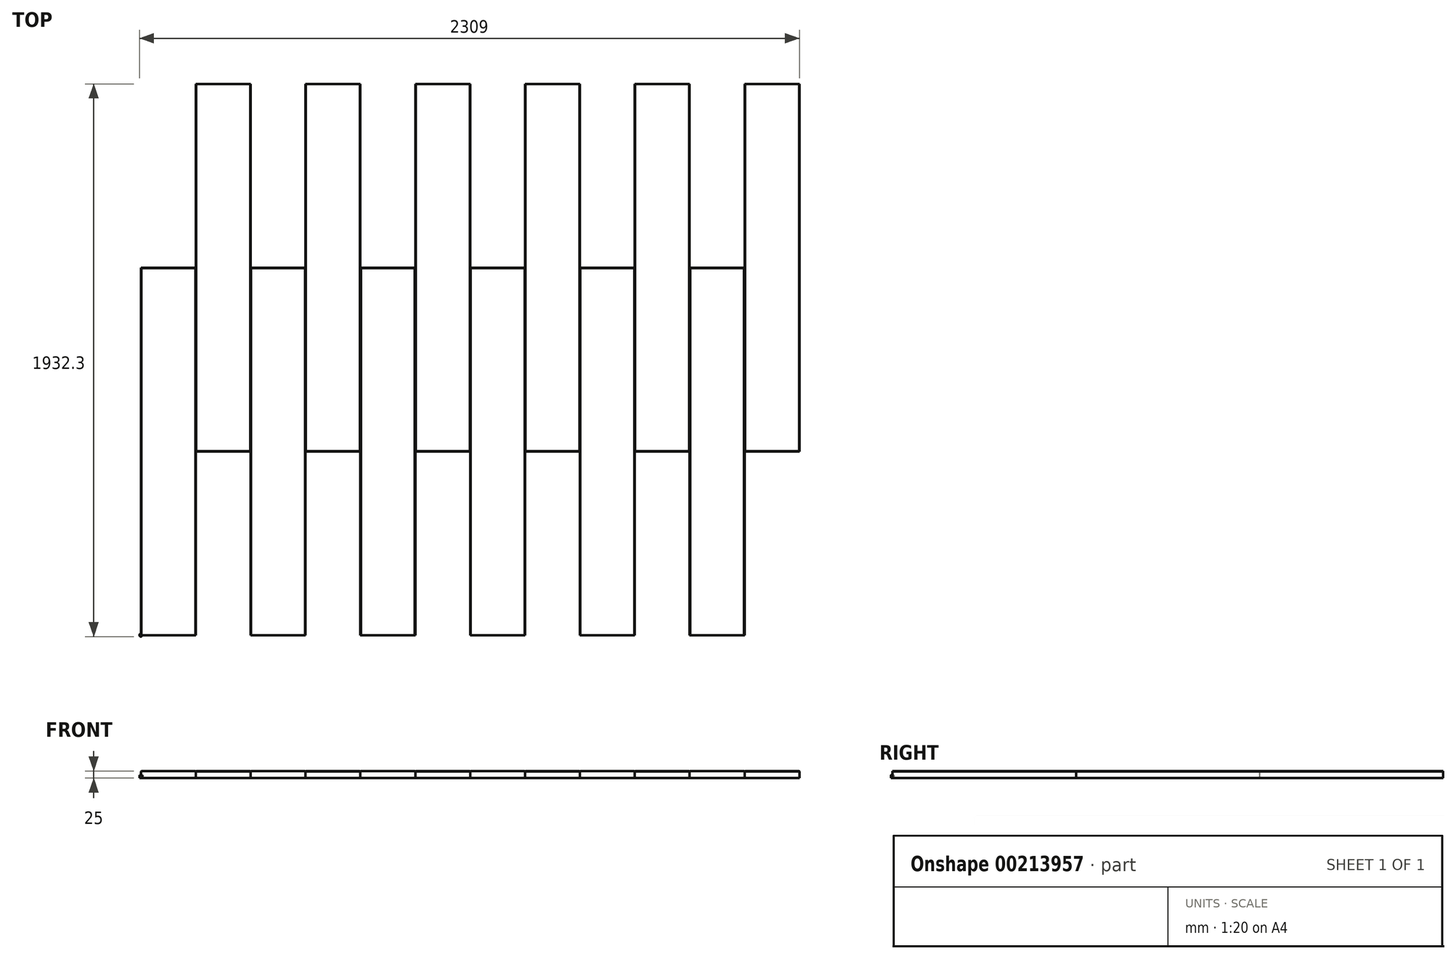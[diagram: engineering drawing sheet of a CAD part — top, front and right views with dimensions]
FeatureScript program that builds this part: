
annotation { "Feature Type Name" : "Feature", "Feature Type Description" : "" }
export const myFeature = defineFeature(function(context is Context, id is Id, definition is map)
    precondition{}
    {
        {
            var Q0;
            Q0=qCreatedBy(makeId("Top.planeOp"),FACE);
            var sketch = newSketch(context, id + "F0", { "sketchPlane" : qUnion([Q0])});
            skCircle(sketch, "E0", {"center": v(0, 0) * mm, "radius": 5 * mm});
            skSolve(sketch);
        }
        {
            var Q0;
            Q0 = qSketchRegion(id + "F0", true);
            extrude(context, id + "F1", {"entities" : qUnion([Q0]), "depth" : 10 * mm});
        }
        {
            var Q0;
            Q0=qCreatedBy(makeId("Top.planeOp"),FACE);
            var sketch = newSketch(context, id + "F2", { "sketchPlane" : qUnion([Q0])});
            skLineSegment(sketch, "E1.bottom", {"start": v(0, 0) * mm, "end": v(192, 0) * mm});
            skLineSegment(sketch, "E1.top", {"start": v(0, 1284.9) * mm, "end": v(192, 1284.9) * mm});
            skLineSegment(sketch, "E1.left", {"start": v(0, 0) * mm, "end": v(0, 1284.9) * mm});
            skLineSegment(sketch, "E1.right", {"start": v(192, 0) * mm, "end": v(192, 1284.9) * mm});
            skLineSegment(sketch, "E2.bottom", {"start": v(192, 642.4) * mm, "end": v(384, 642.4) * mm});
            skLineSegment(sketch, "E2.top", {"start": v(192, 1927.3) * mm, "end": v(384, 1927.3) * mm});
            skLineSegment(sketch, "E2.left", {"start": v(192, 642.4) * mm, "end": v(192, 1927.3) * mm});
            skLineSegment(sketch, "E2.right", {"start": v(384, 642.4) * mm, "end": v(384, 1927.3) * mm});
            skLineSegment(sketch, "E3.1.0.0", {"start": v(576, 1927.3) * mm, "end": v(768, 1927.3) * mm});
            skLineSegment(sketch, "E3.1.0.1", {"start": v(576, 0) * mm, "end": v(576, 1284.9) * mm});
            skLineSegment(sketch, "E3.1.0.2", {"start": v(384, 0) * mm, "end": v(384, 1284.9) * mm});
            skLineSegment(sketch, "E3.1.0.3", {"start": v(768, 642.4) * mm, "end": v(768, 1927.3) * mm});
            skLineSegment(sketch, "E3.1.0.4", {"start": v(576, 642.4) * mm, "end": v(576, 1927.3) * mm});
            skLineSegment(sketch, "E3.1.0.5", {"start": v(384, 1284.9) * mm, "end": v(576, 1284.9) * mm});
            skLineSegment(sketch, "E3.1.0.6", {"start": v(576, 642.4) * mm, "end": v(768, 642.4) * mm});
            skLineSegment(sketch, "E3.1.0.7", {"start": v(384, 0) * mm, "end": v(576, 0) * mm});
            skLineSegment(sketch, "E3.2.0.0", {"start": v(960, 1927.3) * mm, "end": v(1152, 1927.3) * mm});
            skLineSegment(sketch, "E3.2.0.1", {"start": v(960, 0) * mm, "end": v(960, 1284.9) * mm});
            skLineSegment(sketch, "E3.2.0.2", {"start": v(768, 0) * mm, "end": v(768, 1284.9) * mm});
            skLineSegment(sketch, "E3.2.0.3", {"start": v(1152, 642.4) * mm, "end": v(1152, 1927.3) * mm});
            skLineSegment(sketch, "E3.2.0.4", {"start": v(960, 642.4) * mm, "end": v(960, 1927.3) * mm});
            skLineSegment(sketch, "E3.2.0.5", {"start": v(768, 1284.9) * mm, "end": v(960, 1284.9) * mm});
            skLineSegment(sketch, "E3.2.0.6", {"start": v(960, 642.4) * mm, "end": v(1152, 642.4) * mm});
            skLineSegment(sketch, "E3.2.0.7", {"start": v(768, 0) * mm, "end": v(960, 0) * mm});
            skLineSegment(sketch, "E3.3.0.0", {"start": v(1344, 1927.3) * mm, "end": v(1536, 1927.3) * mm});
            skLineSegment(sketch, "E3.3.0.1", {"start": v(1344, 0) * mm, "end": v(1344, 1284.9) * mm});
            skLineSegment(sketch, "E3.3.0.2", {"start": v(1152, 0) * mm, "end": v(1152, 1284.9) * mm});
            skLineSegment(sketch, "E3.3.0.3", {"start": v(1536, 642.4) * mm, "end": v(1536, 1927.3) * mm});
            skLineSegment(sketch, "E3.3.0.4", {"start": v(1344, 642.4) * mm, "end": v(1344, 1927.3) * mm});
            skLineSegment(sketch, "E3.3.0.5", {"start": v(1152, 1284.9) * mm, "end": v(1344, 1284.9) * mm});
            skLineSegment(sketch, "E3.3.0.6", {"start": v(1344, 642.4) * mm, "end": v(1536, 642.4) * mm});
            skLineSegment(sketch, "E3.3.0.7", {"start": v(1152, 0) * mm, "end": v(1344, 0) * mm});
            skLineSegment(sketch, "E3.4.0.0", {"start": v(1728, 1927.3) * mm, "end": v(1920, 1927.3) * mm});
            skLineSegment(sketch, "E3.4.0.1", {"start": v(1728, 0) * mm, "end": v(1728, 1284.9) * mm});
            skLineSegment(sketch, "E3.4.0.2", {"start": v(1536, 0) * mm, "end": v(1536, 1284.9) * mm});
            skLineSegment(sketch, "E3.4.0.3", {"start": v(1920, 642.4) * mm, "end": v(1920, 1927.3) * mm});
            skLineSegment(sketch, "E3.4.0.4", {"start": v(1728, 642.4) * mm, "end": v(1728, 1927.3) * mm});
            skLineSegment(sketch, "E3.4.0.5", {"start": v(1536, 1284.9) * mm, "end": v(1728, 1284.9) * mm});
            skLineSegment(sketch, "E3.4.0.6", {"start": v(1728, 642.4) * mm, "end": v(1920, 642.4) * mm});
            skLineSegment(sketch, "E3.4.0.7", {"start": v(1536, 0) * mm, "end": v(1728, 0) * mm});
            skLineSegment(sketch, "E3.5.0.0", {"start": v(2112, 1927.3) * mm, "end": v(2304, 1927.3) * mm});
            skLineSegment(sketch, "E3.5.0.1", {"start": v(2112, 0) * mm, "end": v(2112, 1284.9) * mm});
            skLineSegment(sketch, "E3.5.0.2", {"start": v(1920, 0) * mm, "end": v(1920, 1284.9) * mm});
            skLineSegment(sketch, "E3.5.0.3", {"start": v(2304, 642.4) * mm, "end": v(2304, 1927.3) * mm});
            skLineSegment(sketch, "E3.5.0.4", {"start": v(2112, 642.4) * mm, "end": v(2112, 1927.3) * mm});
            skLineSegment(sketch, "E3.5.0.5", {"start": v(1920, 1284.9) * mm, "end": v(2112, 1284.9) * mm});
            skLineSegment(sketch, "E3.5.0.6", {"start": v(2112, 642.4) * mm, "end": v(2304, 642.4) * mm});
            skLineSegment(sketch, "E3.5.0.7", {"start": v(1920, 0) * mm, "end": v(2112, 0) * mm});
            skLineSegment(sketch, "E3.direction1", {"start": v(0, 0) * mm, "end": v(384, 0) * mm, "construction": true});
            skSolve(sketch);
        }
        {
            var Q0;
            Q0 = qSketchRegion(id + "F2", true);
            extrude(context, id + "F3", {"entities" : qUnion([Q0]), "operationType" : NewBodyOperationType.ADD, "depth" : 25 * mm});
        }
        {
            var Q0;
            Q0=makeQuery(id+"F3.opExtrude","SWEPT_FACE",FACE,{"disambiguationData":[OSD([sQuery(id+"F2.wireOp",EDGE,"E1.bottom")])]});
            var sketch = newSketch(context, id + "F4", { "sketchPlane" : qUnion([Q0])});
            skLineSegment(sketch, "E4", {"start": v(0, 23.5) * mm, "end": v(1.5, 25) * mm});
            skLineSegment(sketch, "E5", {"start": v(1.5, 25) * mm, "end": v(-1.5, 25) * mm});
            skLineSegment(sketch, "E6", {"start": v(-1.5, 25) * mm, "end": v(0, 23.5) * mm});
            skLineSegment(sketch, "E7.1.0.0", {"start": v(193.5, 25) * mm, "end": v(190.5, 25) * mm});
            skLineSegment(sketch, "E7.1.0.1", {"start": v(190.5, 25) * mm, "end": v(192, 23.5) * mm});
            skLineSegment(sketch, "E7.1.0.2", {"start": v(192, 23.5) * mm, "end": v(193.5, 25) * mm});
            skLineSegment(sketch, "E7.2.0.0", {"start": v(385.5, 25) * mm, "end": v(382.5, 25) * mm});
            skLineSegment(sketch, "E7.2.0.1", {"start": v(382.5, 25) * mm, "end": v(384, 23.5) * mm});
            skLineSegment(sketch, "E7.2.0.2", {"start": v(384, 23.5) * mm, "end": v(385.5, 25) * mm});
            skLineSegment(sketch, "E7.direction1", {"start": v(0, 23.5) * mm, "end": v(192, 23.5) * mm, "construction": true});
            skLineSegment(sketch, "E8.0.3.0", {"start": v(577.5, 25) * mm, "end": v(574.5, 25) * mm});
            skLineSegment(sketch, "E8.3.3.0", {"start": v(574.5, 25) * mm, "end": v(576, 23.5) * mm});
            skLineSegment(sketch, "E8.6.3.0", {"start": v(576, 23.5) * mm, "end": v(577.5, 25) * mm});
            skLineSegment(sketch, "E8.0.4.0", {"start": v(769.5, 25) * mm, "end": v(766.5, 25) * mm});
            skLineSegment(sketch, "E8.3.4.0", {"start": v(766.5, 25) * mm, "end": v(768, 23.5) * mm});
            skLineSegment(sketch, "E8.6.4.0", {"start": v(768, 23.5) * mm, "end": v(769.5, 25) * mm});
            skLineSegment(sketch, "E8.0.5.0", {"start": v(961.5, 25) * mm, "end": v(958.5, 25) * mm});
            skLineSegment(sketch, "E8.3.5.0", {"start": v(958.5, 25) * mm, "end": v(960, 23.5) * mm});
            skLineSegment(sketch, "E8.6.5.0", {"start": v(960, 23.5) * mm, "end": v(961.5, 25) * mm});
            skLineSegment(sketch, "E8.0.6.0", {"start": v(1153.5, 25) * mm, "end": v(1150.5, 25) * mm});
            skLineSegment(sketch, "E8.3.6.0", {"start": v(1150.5, 25) * mm, "end": v(1152, 23.5) * mm});
            skLineSegment(sketch, "E8.6.6.0", {"start": v(1152, 23.5) * mm, "end": v(1153.5, 25) * mm});
            skLineSegment(sketch, "E8.0.7.0", {"start": v(1345.5, 25) * mm, "end": v(1342.5, 25) * mm});
            skLineSegment(sketch, "E8.3.7.0", {"start": v(1342.5, 25) * mm, "end": v(1344, 23.5) * mm});
            skLineSegment(sketch, "E8.6.7.0", {"start": v(1344, 23.5) * mm, "end": v(1345.5, 25) * mm});
            skLineSegment(sketch, "E8.0.8.0", {"start": v(1537.5, 25) * mm, "end": v(1534.5, 25) * mm});
            skLineSegment(sketch, "E8.3.8.0", {"start": v(1534.5, 25) * mm, "end": v(1536, 23.5) * mm});
            skLineSegment(sketch, "E8.6.8.0", {"start": v(1536, 23.5) * mm, "end": v(1537.5, 25) * mm});
            skLineSegment(sketch, "E8.0.9.0", {"start": v(1729.5, 25) * mm, "end": v(1726.5, 25) * mm});
            skLineSegment(sketch, "E8.3.9.0", {"start": v(1726.5, 25) * mm, "end": v(1728, 23.5) * mm});
            skLineSegment(sketch, "E8.6.9.0", {"start": v(1728, 23.5) * mm, "end": v(1729.5, 25) * mm});
            skLineSegment(sketch, "E8.0.10.0", {"start": v(1921.5, 25) * mm, "end": v(1918.5, 25) * mm});
            skLineSegment(sketch, "E8.3.10.0", {"start": v(1918.5, 25) * mm, "end": v(1920, 23.5) * mm});
            skLineSegment(sketch, "E8.6.10.0", {"start": v(1920, 23.5) * mm, "end": v(1921.5, 25) * mm});
            skLineSegment(sketch, "E8.0.11.0", {"start": v(2113.5, 25) * mm, "end": v(2110.5, 25) * mm});
            skLineSegment(sketch, "E8.3.11.0", {"start": v(2110.5, 25) * mm, "end": v(2112, 23.5) * mm});
            skLineSegment(sketch, "E8.6.11.0", {"start": v(2112, 23.5) * mm, "end": v(2113.5, 25) * mm});
            skLineSegment(sketch, "E8.0.12.0", {"start": v(2305.5, 25) * mm, "end": v(2302.5, 25) * mm});
            skLineSegment(sketch, "E8.3.12.0", {"start": v(2302.5, 25) * mm, "end": v(2304, 23.5) * mm});
            skLineSegment(sketch, "E8.6.12.0", {"start": v(2304, 23.5) * mm, "end": v(2305.5, 25) * mm});
            skSolve(sketch);
        }
        {
            var Q0;
            Q0 = qSketchRegion(id + "F4", true);
            extrude(context, id + "F5", {"entities" : qUnion([Q0]), "operationType" : NewBodyOperationType.REMOVE, "endBound" : BoundingType.THROUGH_ALL, "oppositeDirection" : true, "depth" : 25 * mm});
        }
        {
            var Q0;
            Q0=makeQuery(id+"F3.opExtrude","CAP_EDGE",EDGE,{"disambiguationData":[OSD([sQuery(id+"F2.wireOp",EDGE,"E2.bottom")])],"isStart":false});
            var Q1;
            Q1=makeQuery(id+"F3.opExtrude","CAP_EDGE",EDGE,{"disambiguationData":[OSD([sQuery(id+"F2.wireOp",EDGE,"E3.1.0.6")])],"isStart":false});
            var Q2;
            Q2=makeQuery(id+"F3.opExtrude","CAP_EDGE",EDGE,{"disambiguationData":[OSD([sQuery(id+"F2.wireOp",EDGE,"E3.2.0.6")])],"isStart":false});
            var Q3;
            Q3=makeQuery(id+"F3.opExtrude","CAP_EDGE",EDGE,{"disambiguationData":[OSD([sQuery(id+"F2.wireOp",EDGE,"E3.3.0.6")])],"isStart":false});
            var Q4;
            Q4=makeQuery(id+"F3.opExtrude","CAP_EDGE",EDGE,{"disambiguationData":[OSD([sQuery(id+"F2.wireOp",EDGE,"E3.4.0.6")])],"isStart":false});
            var Q5;
            Q5=makeQuery(id+"F3.opExtrude","CAP_EDGE",EDGE,{"disambiguationData":[OSD([sQuery(id+"F2.wireOp",EDGE,"E3.5.0.6")])],"isStart":false});
            var Q6;
            Q6=makeQuery(id+"F3.opExtrude","CAP_EDGE",EDGE,{"disambiguationData":[OSD([sQuery(id+"F2.wireOp",EDGE,"E1.top")])],"isStart":false});
            var Q7;
            Q7=makeQuery(id+"F3.opExtrude","CAP_EDGE",EDGE,{"disambiguationData":[OSD([sQuery(id+"F2.wireOp",EDGE,"E3.1.0.5")])],"isStart":false});
            var Q8;
            Q8=makeQuery(id+"F3.opExtrude","CAP_EDGE",EDGE,{"disambiguationData":[OSD([sQuery(id+"F2.wireOp",EDGE,"E3.2.0.5")])],"isStart":false});
            var Q9;
            Q9=makeQuery(id+"F3.opExtrude","CAP_EDGE",EDGE,{"disambiguationData":[OSD([sQuery(id+"F2.wireOp",EDGE,"E3.3.0.5")])],"isStart":false});
            var Q10;
            Q10=makeQuery(id+"F3.opExtrude","CAP_EDGE",EDGE,{"disambiguationData":[OSD([sQuery(id+"F2.wireOp",EDGE,"E3.4.0.5")])],"isStart":false});
            var Q11;
            Q11=makeQuery(id+"F3.opExtrude","CAP_EDGE",EDGE,{"disambiguationData":[OSD([sQuery(id+"F2.wireOp",EDGE,"E3.5.0.5")])],"isStart":false});
            chamfer(context, id + "F6", {"entities" : qUnion([Q0, Q1, Q2, Q3, Q4, Q5, Q6, Q7, Q8, Q9, Q10, Q11]), "width" : 1.5 * mm, "tangentPropagation" : true});
        }
    });
